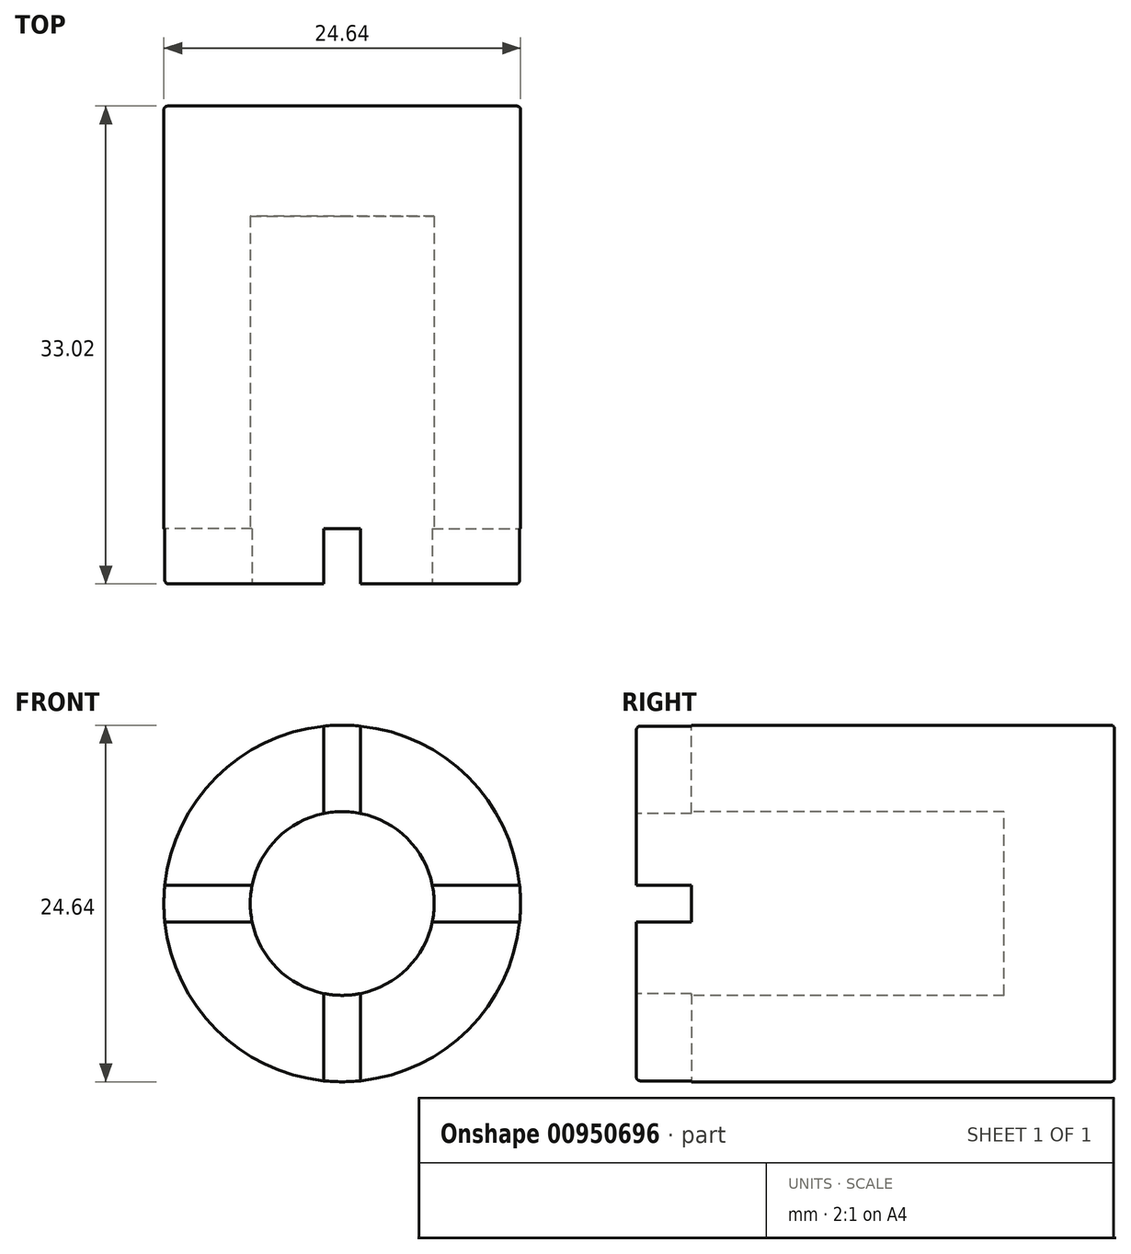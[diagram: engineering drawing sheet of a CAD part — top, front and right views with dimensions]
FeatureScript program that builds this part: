
annotation { "Feature Type Name" : "Feature", "Feature Type Description" : "" }
export const myFeature = defineFeature(function(context is Context, id is Id, definition is map)
    precondition{}
    {
        {
            var Q0;
            Q0=qCreatedBy(makeId("Front.planeOp"),FACE);
            var sketch = newSketch(context, id + "F0", { "sketchPlane" : qUnion([Q0])});
            skCircle(sketch, "E0", {"center": v(0, 0) * mm, "radius": 12.32 * mm});
            skSolve(sketch);
        }
        {
            var Q0;
            Q0=qSketchRegion(id+"F0",true);
            extrude(context, id + "F1", {"entities" : qUnion([Q0]), "depth" : 33.02 * mm, "offsetDistance" : 25.4 * mm});
        }
        {
            var Q0;
            Q0=makeQuery(id+"F1.opExtrude","CAP_FACE",FACE,{"disambiguationData":[OSD([sQuery(id+"F0.wireOp",EDGE,"E0")])],"isStart":true});
            var sketch = newSketch(context, id + "F2", { "sketchPlane" : qUnion([Q0])});
            skLineSegment(sketch, "E1.bottom", {"start": v(30.22, -6.99) * mm, "end": v(-30.22, -6.99) * mm});
            skLineSegment(sketch, "E1.top", {"start": v(30.22, 6.99) * mm, "end": v(-30.22, 6.99) * mm});
            skLineSegment(sketch, "E1.left", {"start": v(30.22, -6.99) * mm, "end": v(30.22, 6.99) * mm});
            skLineSegment(sketch, "E1.right", {"start": v(-30.22, -6.99) * mm, "end": v(-30.22, 6.99) * mm});
            skPoint(sketch, "E1.middle", {"position": v(0, 0) * mm});
            skSolve(sketch);
        }
        {
            var Q0;
            Q0=makeQuery(id+"F1.opExtrude","CAP_FACE",FACE,{"disambiguationData":[OSD([sQuery(id+"F0.wireOp",EDGE,"E0")])],"isStart":false});
            var sketch = newSketch(context, id + "F3", { "sketchPlane" : qUnion([Q0])});
            skCircle(sketch, "E2", {"center": v(0, 0) * mm, "radius": 6.35 * mm});
            skSolve(sketch);
        }
        {
            var Q0;
            Q0=qSketchRegion(id+"F3",true);
            extrude(context, id + "F4", {"entities" : qUnion([Q0]), "operationType" : NewBodyOperationType.REMOVE, "oppositeDirection" : true, "depth" : 25.4 * mm, "offsetDistance" : 25.4 * mm});
        }
        {
            var Q0;
            Q0=makeQuery(id+"F3bAOIRODMrbrFh_1.boolean.opBoolean","INTERSECT",EDGE,{"disambiguationData":[OD(1.0)],"derivedFrom":[makeQuery(id+"F1.opExtrude","SWEPT_FACE",FACE,{"disambiguationData":[OSD([sQuery(id+"F0.wireOp",EDGE,"E0")])]}),makeQuery(id+"F3bAOIRODMrbrFh_1.opExtrude","SWEPT_FACE",FACE,{"disambiguationData":[OSD([sQuery(id+"F2.wireOp",EDGE,"E1.top")])]})]});
            var Q1;
            Q1=makeQuery(id+"F3bAOIRODMrbrFh_1.boolean.opBoolean","COPY",EDGE,{"derivedFrom":makeQuery(id+"F3bAOIRODMrbrFh_1.opExtrude","CAP_EDGE",EDGE,{"disambiguationData":[OSD([sQuery(id+"F2.wireOp",EDGE,"E1.top")])],"isStart":true})});
            var Q2;
            {var subQ0=sQuery(id+"F0.wireOp",EDGE,"E0");Q2=makeQuery(id+"F3bAOIRODMrbrFh_1.boolean.opBoolean","SPLIT",EDGE,{"disambiguationData":[TD([makeQuery(id+"F3bAOIRODMrbrFh_1.opExtrude","SWEPT_FACE",FACE,{"disambiguationData":[OSD([sQuery(id+"F2.wireOp",EDGE,"E1.top")])]})])],"derivedFrom":makeQuery(id+"F1.opExtrude","CAP_EDGE",EDGE,{"disambiguationData":[OSD([subQ0])],"isStart":true})});}
            var Q3;
            Q3=makeQuery(id+"F3bAOIRODMrbrFh_1.boolean.opBoolean","INTERSECT",EDGE,{"disambiguationData":[OD(0.0)],"derivedFrom":[makeQuery(id+"F1.opExtrude","SWEPT_FACE",FACE,{"disambiguationData":[OSD([sQuery(id+"F0.wireOp",EDGE,"E0")])]}),makeQuery(id+"F3bAOIRODMrbrFh_1.opExtrude","SWEPT_FACE",FACE,{"disambiguationData":[OSD([sQuery(id+"F2.wireOp",EDGE,"E1.top")])]})]});
            var Q4;
            Q4=makeQuery(id+"F3bAOIRODMrbrFh_1.boolean.opBoolean","INTERSECT",EDGE,{"disambiguationData":[OD(1.0)],"derivedFrom":[makeQuery(id+"F1.opExtrude","SWEPT_FACE",FACE,{"disambiguationData":[OSD([sQuery(id+"F0.wireOp",EDGE,"E0")])]}),makeQuery(id+"F3bAOIRODMrbrFh_1.opExtrude","SWEPT_FACE",FACE,{"disambiguationData":[OSD([sQuery(id+"F2.wireOp",EDGE,"E1.bottom")])]})]});
            var Q5;
            Q5=makeQuery(id+"F3bAOIRODMrbrFh_1.boolean.opBoolean","INTERSECT",EDGE,{"disambiguationData":[OD(0.0)],"derivedFrom":[makeQuery(id+"F1.opExtrude","SWEPT_FACE",FACE,{"disambiguationData":[OSD([sQuery(id+"F0.wireOp",EDGE,"E0")])]}),makeQuery(id+"F3bAOIRODMrbrFh_1.opExtrude","SWEPT_FACE",FACE,{"disambiguationData":[OSD([sQuery(id+"F2.wireOp",EDGE,"E1.bottom")])]})]});
            var Q6;
            Q6=makeQuery(id+"F3bAOIRODMrbrFh_1.boolean.opBoolean","COPY",EDGE,{"derivedFrom":makeQuery(id+"F3bAOIRODMrbrFh_1.opExtrude","CAP_EDGE",EDGE,{"disambiguationData":[OSD([sQuery(id+"F2.wireOp",EDGE,"E1.bottom")])],"isStart":true})});
            var Q7;
            {var subQ0=sQuery(id+"F0.wireOp",EDGE,"E0");Q7=makeQuery(id+"F3bAOIRODMrbrFh_1.boolean.opBoolean","SPLIT",EDGE,{"disambiguationData":[TD([makeQuery(id+"F3bAOIRODMrbrFh_1.opExtrude","SWEPT_FACE",FACE,{"disambiguationData":[OSD([sQuery(id+"F2.wireOp",EDGE,"E1.bottom")])]})])],"derivedFrom":makeQuery(id+"F1.opExtrude","CAP_EDGE",EDGE,{"disambiguationData":[OSD([subQ0])],"isStart":true})});}
            var Q8;
            Q8=makeQuery(id+"F1.opExtrude","CAP_EDGE",EDGE,{"disambiguationData":[OSD([sQuery(id+"F0.wireOp",EDGE,"E0")])],"isStart":false});
            fillet(context, id + "F5", {"entities" : qUnion([Q0, Q1, Q2, Q3, Q4, Q5, Q6, Q7, Q8]), "radius" : 0.25 * mm, "tangentPropagation" : true, "allowEdgeOverflow" : false});
        }
        {
            var Q0;
            Q0=makeQuery(id+"F1.opExtrude","CAP_FACE",FACE,{"disambiguationData":[OSD([sQuery(id+"F0.wireOp",EDGE,"E0")])],"isStart":false});
            var sketch = newSketch(context, id + "F6", { "sketchPlane" : qUnion([Q0])});
            skLineSegment(sketch, "E3.left", {"start": v(1.27, 6.22) * mm, "end": v(1.27, 12.25) * mm});
            skLineSegment(sketch, "E3.right", {"start": v(-1.27, 6.22) * mm, "end": v(-1.27, 12.25) * mm});
            skPoint(sketch, "E3.middle", {"position": v(0, 8.9) * mm});
            skArc(sketch, "E4", {"start": v(1.27, 6.22) * mm, "mid": v(0, 6.35) * mm, "end": v(-1.27, 6.22) * mm});
            skArc(sketch, "E5", {"start": v(1.27, 12.25) * mm, "mid": v(0, 12.32) * mm, "end": v(-1.27, 12.25) * mm});
            skArc(sketch, "E6.1.0", {"start": v(-12.25, 1.27) * mm, "mid": v(-12.32, 0) * mm, "end": v(-12.25, -1.27) * mm});
            skLineSegment(sketch, "E6.1.1", {"start": v(-6.22, 1.27) * mm, "end": v(-12.25, 1.27) * mm});
            skLineSegment(sketch, "E6.1.2", {"start": v(-6.22, -1.27) * mm, "end": v(-12.25, -1.27) * mm});
            skArc(sketch, "E6.1.3", {"start": v(-6.22, 1.27) * mm, "mid": v(-6.35, 0) * mm, "end": v(-6.22, -1.27) * mm});
            skArc(sketch, "E6.2.0", {"start": v(-1.27, -12.25) * mm, "mid": v(0, -12.32) * mm, "end": v(1.27, -12.25) * mm});
            skLineSegment(sketch, "E6.2.1", {"start": v(-1.27, -6.22) * mm, "end": v(-1.27, -12.25) * mm});
            skLineSegment(sketch, "E6.2.2", {"start": v(1.27, -6.22) * mm, "end": v(1.27, -12.25) * mm});
            skArc(sketch, "E6.2.3", {"start": v(-1.27, -6.22) * mm, "mid": v(0, -6.35) * mm, "end": v(1.27, -6.22) * mm});
            skArc(sketch, "E6.3.0", {"start": v(12.25, -1.27) * mm, "mid": v(12.32, 0) * mm, "end": v(12.25, 1.27) * mm});
            skLineSegment(sketch, "E6.3.1", {"start": v(6.22, -1.27) * mm, "end": v(12.25, -1.27) * mm});
            skLineSegment(sketch, "E6.3.2", {"start": v(6.22, 1.27) * mm, "end": v(12.25, 1.27) * mm});
            skArc(sketch, "E6.3.3", {"start": v(6.22, -1.27) * mm, "mid": v(6.35, 0) * mm, "end": v(6.22, 1.27) * mm});
            skSolve(sketch);
        }
        {
            var Q0;
            Q0 = qSketchRegion(id + "F6", true);
            extrude(context, id + "F7", {"entities" : qUnion([Q0]), "operationType" : NewBodyOperationType.REMOVE, "oppositeDirection" : true, "depth" : 3.8 * mm, "offsetDistance" : 25.4 * mm});
        }
    });
